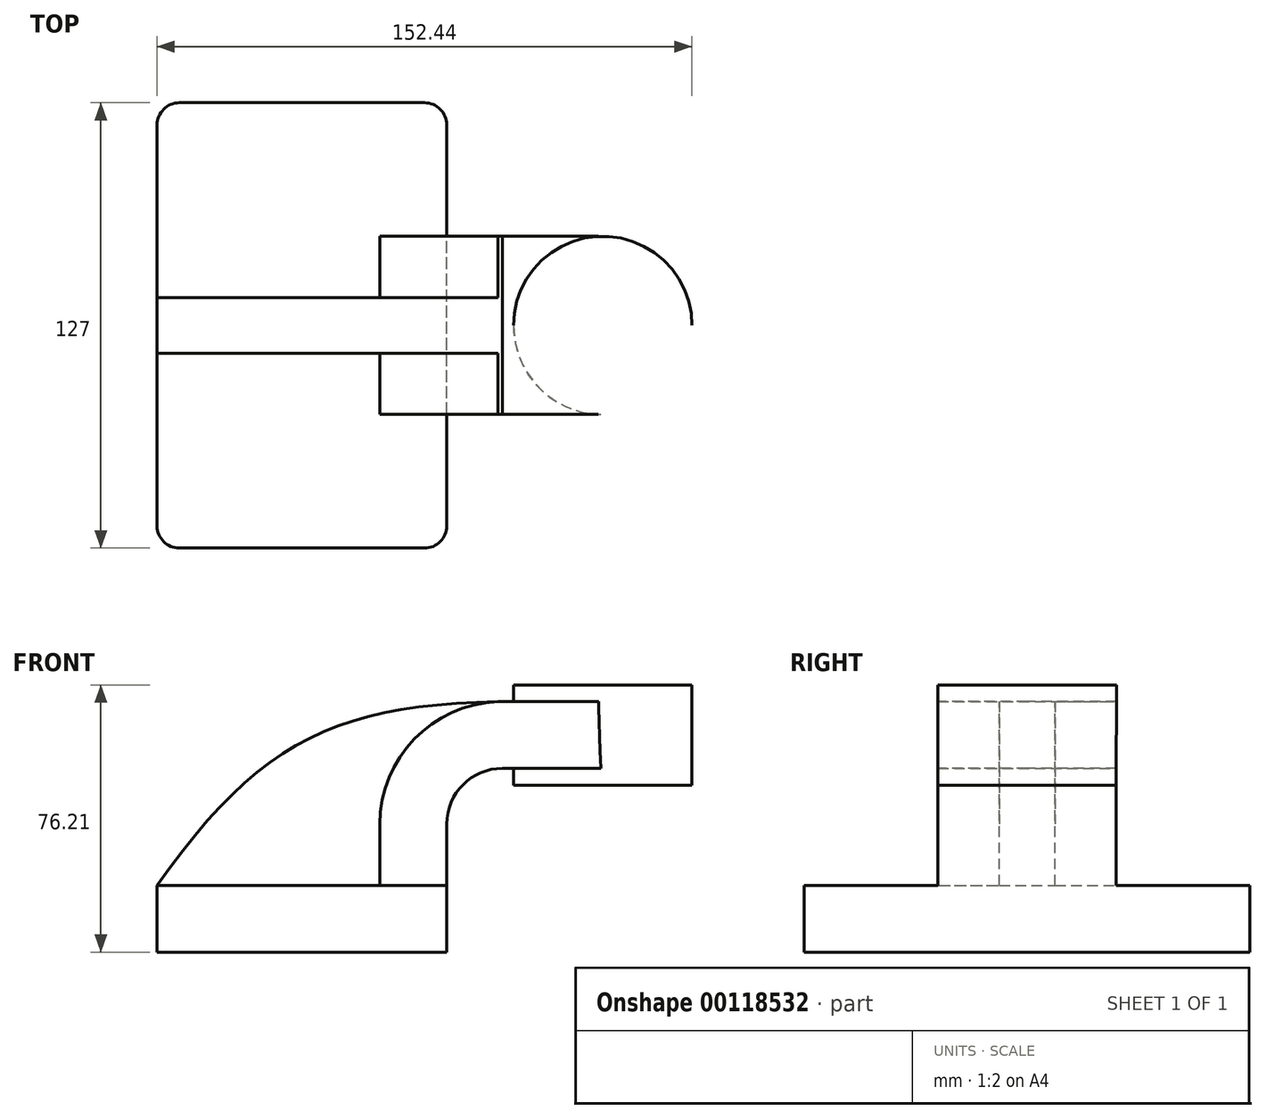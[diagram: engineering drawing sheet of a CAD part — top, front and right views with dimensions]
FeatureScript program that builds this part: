
annotation { "Feature Type Name" : "Feature", "Feature Type Description" : "" }
export const myFeature = defineFeature(function(context is Context, id is Id, definition is map)
    precondition{}
    {
        {
            var Q0;
            Q0=qCreatedBy(makeId("Front.planeOp"),FACE);
            var sketch = newSketch(context, id + "F0", { "sketchPlane" : qUnion([Q0])});
            skLineSegment(sketch, "E0.bottom", {"start": v(41.28, -9.52) * mm, "end": v(-41.28, -9.53) * mm});
            skLineSegment(sketch, "E0.top", {"start": v(41.28, 9.53) * mm, "end": v(-41.28, 9.52) * mm});
            skLineSegment(sketch, "E0.left", {"start": v(41.28, -9.52) * mm, "end": v(41.28, 9.53) * mm});
            skLineSegment(sketch, "E0.right", {"start": v(-41.28, -9.53) * mm, "end": v(-41.28, 9.52) * mm});
            skPoint(sketch, "E0.middle", {"position": v(0, 0) * mm});
            skLineSegment(sketch, "E1.bottom", {"start": v(60.36, 38.1) * mm, "end": v(111.16, 38.1) * mm});
            skLineSegment(sketch, "E1.top", {"start": v(60.36, 66.68) * mm, "end": v(111.16, 66.68) * mm});
            skLineSegment(sketch, "E1.left", {"start": v(60.36, 38.1) * mm, "end": v(60.36, 66.67) * mm});
            skLineSegment(sketch, "E1.right", {"start": v(111.16, 38.1) * mm, "end": v(111.16, 66.67) * mm});
            skPoint(sketch, "E1.middle", {"position": v(85.76, 52.39) * mm});
            skLineSegment(sketch, "E2", {"start": v(41.28, 9.53) * mm, "end": v(41.28, 27) * mm});
            skArc(sketch, "E3", {"start": v(41.28, 27) * mm, "mid": v(45.92, 38.23) * mm, "end": v(57.15, 42.88) * mm});
            skLineSegment(sketch, "E4", {"start": v(57.15, 42.88) * mm, "end": v(85.72, 42.88) * mm});
            skLineSegment(sketch, "E5.0", {"start": v(57.15, 61.93) * mm, "end": v(85.72, 61.93) * mm});
            skArc(sketch, "E5.1", {"start": v(22.23, 27) * mm, "mid": v(32.45, 51.7) * mm, "end": v(57.15, 61.93) * mm});
            skLineSegment(sketch, "E5.2", {"start": v(22.23, 9.53) * mm, "end": v(22.23, 27) * mm});
            skFitSpline(sketch, "E6", {"points": [v(-41.28, 9.53) * mm, v(57.15, 61.93) * mm], "startDerivative": vector(86.37, 121.91) * mm, "endDerivative": vector(145.3, 2.5) * mm});
            skLineSegment(sketch, "E7", {"start": v(85.76, 38.1) * mm, "end": v(85.72, 66.68) * mm});
            skLineSegment(sketch, "E8", {"start": v(85.72, 42.88) * mm, "end": v(85.72, 61.93) * mm});
            skSolve(sketch);
        }
        {
            var Q0;
            Q0=makeQuery(id+"F0.imprint","IMPRINT",FACE,{"disambiguationData":[TD([[makeQuery(id+"F0.imprint","IMPRINT",EDGE,{"derivedFrom":sQuery(id+"F0.wireOp",EDGE,"E0.bottom")}),-1.0]])]});
            extrude(context, id + "F1", {"entities" : qUnion([Q0]), "endBound" : BoundingType.SYMMETRIC, "depth" : 127 * mm});
        }
        {
            var Q0;
            {var subQ1=sQuery(id+"F0.wireOp",EDGE,"E2");Q0=makeQuery(id+"F0.imprint","IMPRINT",FACE,{"disambiguationData":[TD([[makeQuery(id+"F0.imprint","IMPRINT",EDGE,{"derivedFrom":subQ1}),1.0]])]});}
            var Q1;
            {var subQ5=sQuery(id+"F0.wireOp",EDGE,"E8");Q1=makeQuery(id+"F0.imprint","IMPRINT",FACE,{"disambiguationData":[TD([[makeQuery(id+"F0.imprint","IMPRINT",EDGE,{"derivedFrom":subQ5}),1.0]])]});}
            extrude(context, id + "F2", {"entities" : qUnion([Q0, Q1]), "operationType" : NewBodyOperationType.ADD, "endBound" : BoundingType.SYMMETRIC, "depth" : 50.8 * mm});
        }
        {
            var Q0;
            {var subQ3=sQuery(id+"F0.wireOp",EDGE,"E5.2");Q0=makeQuery(id+"F0.imprint","IMPRINT",FACE,{"disambiguationData":[TD([[makeQuery(id+"F0.imprint","IMPRINT",EDGE,{"derivedFrom":subQ3}),1.0]])]});}
            extrude(context, id + "F3", {"entities" : qUnion([Q0]), "operationType" : NewBodyOperationType.ADD, "endBound" : BoundingType.SYMMETRIC, "depth" : 15.88 * mm});
        }
        {
            var Q0;
            {var subQ0=sQuery(id+"F0.wireOp",EDGE,"E1.right");Q0=makeQuery(id+"F0.imprint","IMPRINT",FACE,{"disambiguationData":[TD([[makeQuery(id+"F0.imprint","IMPRINT",EDGE,{"derivedFrom":subQ0}),1.0]])]});}
            var Q1;
            Q1=sQuery(id+"F0.wireOp",EDGE,"E7");
            revolve(context, id + "F4", {"operationType" : NewBodyOperationType.ADD, "entities" : qUnion([Q0]), "axis" : qUnion([Q1]), "revolveType" : RevolveType.FULL});
        }
        {
            var Q0;
            Q0=makeQuery(id+"F1.opExtrude","CAP_EDGE",EDGE,{"disambiguationData":[OSD([sQuery(id+"F0.wireOp",EDGE,"E0.right")])],"isStart":false});
            var Q1;
            Q1=makeQuery(id+"F1.opExtrude","CAP_EDGE",EDGE,{"disambiguationData":[OSD([sQuery(id+"F0.wireOp",EDGE,"E0.left")])],"isStart":false});
            var Q2;
            Q2=makeQuery(id+"F1.opExtrude","CAP_EDGE",EDGE,{"disambiguationData":[OSD([sQuery(id+"F0.wireOp",EDGE,"E0.left")])],"isStart":true});
            var Q3;
            Q3=makeQuery(id+"F1.opExtrude","CAP_EDGE",EDGE,{"disambiguationData":[OSD([sQuery(id+"F0.wireOp",EDGE,"E0.right")])],"isStart":true});
            fillet(context, id + "F5", {"entities" : qUnion([Q0, Q1, Q2, Q3]), "radius" : 6.35 * mm, "tangentPropagation" : true, "allowEdgeOverflow" : false});
        }
    });
